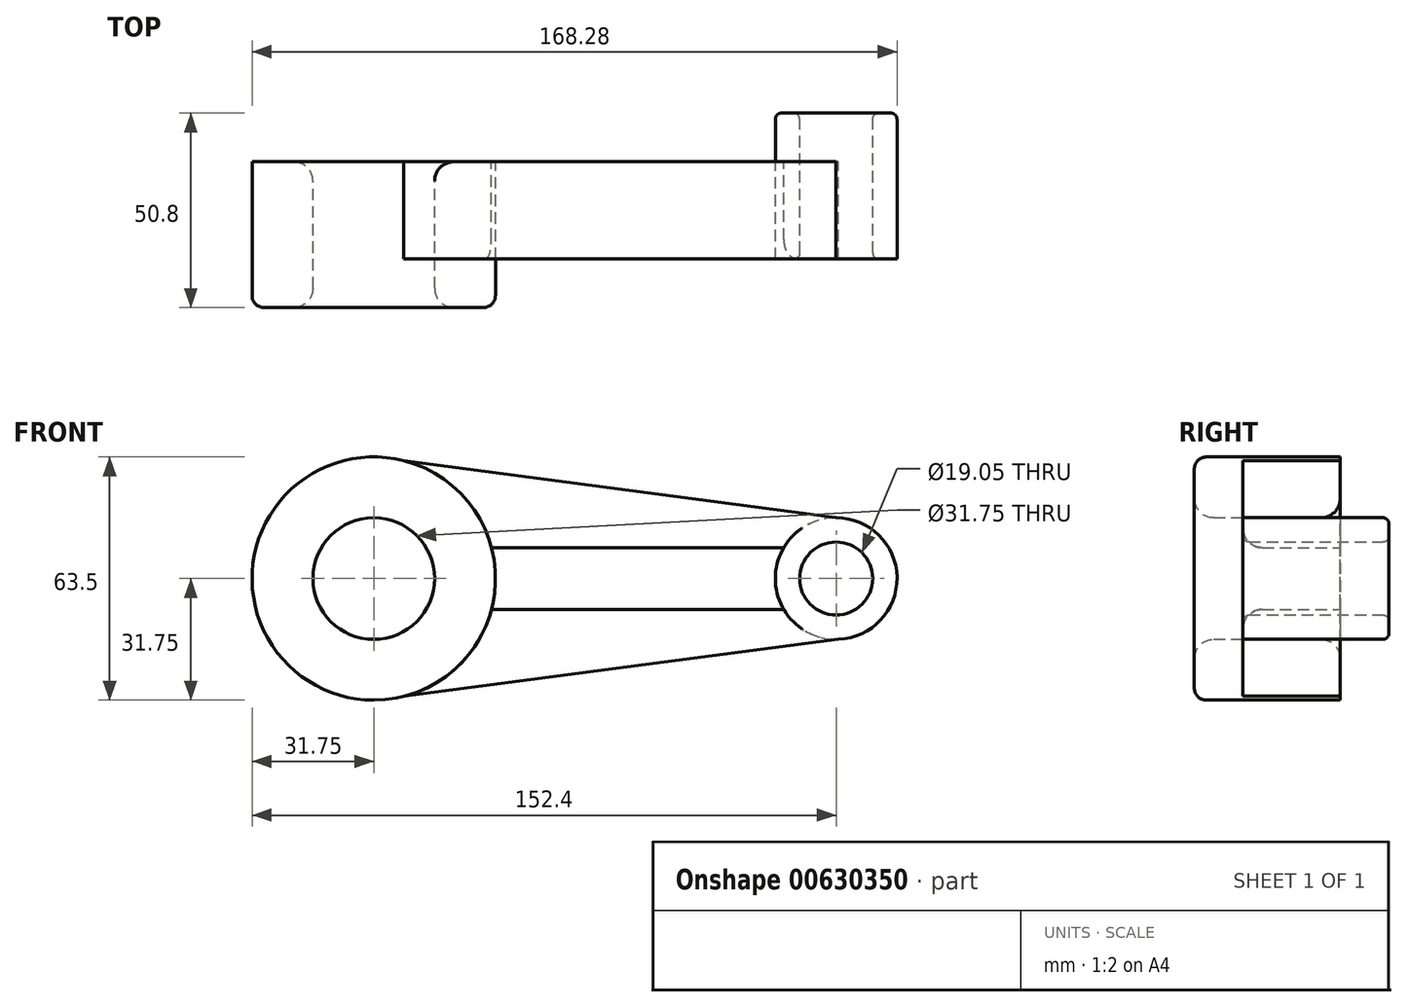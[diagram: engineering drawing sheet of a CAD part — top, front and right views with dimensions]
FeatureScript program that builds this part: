
annotation { "Feature Type Name" : "Feature", "Feature Type Description" : "" }
export const myFeature = defineFeature(function(context is Context, id is Id, definition is map)
    precondition{}
    {
        {
            var Q0;
            Q0=qCreatedBy(makeId("Front.planeOp"),FACE);
            var sketch = newSketch(context, id + "F0", { "sketchPlane" : qUnion([Q0])});
            skCircle(sketch, "E0", {"center": v(0, 0) * mm, "radius": 31.75 * mm});
            skCircle(sketch, "E1", {"center": v(120.65, 0) * mm, "radius": 15.88 * mm});
            skLineSegment(sketch, "E2", {"start": v(0.48, 31.75) * mm, "end": v(120.57, 15.87) * mm});
            skLineSegment(sketch, "E3", {"start": v(121.27, -15.86) * mm, "end": v(0.19, -31.75) * mm});
            skLineSegment(sketch, "E4.0", {"start": v(30.7, -8.06) * mm, "end": v(106.98, -8.06) * mm});
            skLineSegment(sketch, "E5.0", {"start": v(30.7, 8.06) * mm, "end": v(106.98, 8.06) * mm});
            skCircle(sketch, "E6", {"center": v(0, 0) * mm, "radius": 15.88 * mm});
            skCircle(sketch, "E7", {"center": v(120.65, 0) * mm, "radius": 9.53 * mm});
            skSolve(sketch);
        }
        {
            var Q0;
            Q0 = qSketchRegion(id + "F0", true);
            extrude(context, id + "F1", {"entities" : qUnion([Q0]), "depth" : 25.4 * mm, "offsetDistance" : 25.4 * mm});
        }
        {
            var Q0;
            Q0=makeQuery(id+"F1.opExtrude","CAP_FACE",FACE,{"disambiguationData":[OSD([sQuery(id+"F0.wireOp",EDGE,"E0"),sQuery(id+"F0.wireOp",EDGE,"E1"),sQuery(id+"F0.wireOp",EDGE,"E2"),sQuery(id+"F0.wireOp",EDGE,"E3"),sQuery(id+"F0.wireOp",EDGE,"E4.0"),sQuery(id+"F0.wireOp",EDGE,"E5.0"),sQuery(id+"F0.wireOp",EDGE,"E6"),sQuery(id+"F0.wireOp",EDGE,"E7")])],"isStart":false});
            var sketch = newSketch(context, id + "F2", { "sketchPlane" : qUnion([Q0])});
            skCircle(sketch, "E8", {"center": v(0, 0) * mm, "radius": 31.75 * mm});
            skCircle(sketch, "E9", {"center": v(0, 0) * mm, "radius": 15.88 * mm});
            skSolve(sketch);
        }
        {
            var Q0;
            Q0=makeQuery(id+"F1.opExtrude","CAP_FACE",FACE,{"disambiguationData":[OSD([sQuery(id+"F0.wireOp",EDGE,"E0"),sQuery(id+"F0.wireOp",EDGE,"E1"),sQuery(id+"F0.wireOp",EDGE,"E2"),sQuery(id+"F0.wireOp",EDGE,"E3"),sQuery(id+"F0.wireOp",EDGE,"E4.0"),sQuery(id+"F0.wireOp",EDGE,"E5.0"),sQuery(id+"F0.wireOp",EDGE,"E6"),sQuery(id+"F0.wireOp",EDGE,"E7")])],"isStart":true});
            var sketch = newSketch(context, id + "F3", { "sketchPlane" : qUnion([Q0])});
            skCircle(sketch, "E10", {"center": v(-120.65, 0) * mm, "radius": 9.53 * mm});
            skCircle(sketch, "E11", {"center": v(-120.65, 0) * mm, "radius": 15.88 * mm});
            skSolve(sketch);
        }
        {
            var Q0;
            Q0 = qSketchRegion(id + "F3", true);
            extrude(context, id + "F4", {"entities" : qUnion([Q0]), "operationType" : NewBodyOperationType.ADD, "depth" : 12.7 * mm, "offsetDistance" : 25.4 * mm});
        }
        {
            var Q0;
            Q0 = qSketchRegion(id + "F2", true);
            extrude(context, id + "F5", {"entities" : qUnion([Q0]), "operationType" : NewBodyOperationType.ADD, "depth" : 12.7 * mm, "offsetDistance" : 25.4 * mm});
        }
        {
            var Q0;
            Q0=makeQuery(id+"F1.opExtrude","CAP_EDGE",EDGE,{"disambiguationData":[OSD([sQuery(id+"F0.wireOp",EDGE,"E4.0")])],"isStart":false});
            var Q1;
            Q1=makeQuery(id+"F1.opExtrude","CAP_EDGE",EDGE,{"disambiguationData":[OSD([sQuery(id+"F0.wireOp",EDGE,"E5.0")])],"isStart":false});
            var Q2;
            {var subQ3=sQuery(id+"F0.wireOp",EDGE,"E3");var subQ7=sQuery(id+"F2.wireOp",EDGE,"E8");Q2=makeQuery(id+"F5.boolean.opBoolean","SPLIT",EDGE,{"disambiguationData":[TD([makeQuery(id+"F1.opExtrude","SWEPT_FACE",FACE,{"disambiguationData":[OSD([subQ3])]})])],"derivedFrom":makeQuery(id+"F5.opExtrude","CAP_EDGE",EDGE,{"disambiguationData":[OSD([subQ7])],"isStart":true})});}
            var Q3;
            {var subQ0=sQuery(id+"F0.wireOp",EDGE,"E2");var subQ1=sQuery(id+"F2.wireOp",EDGE,"E8");Q3=makeQuery(id+"F5.boolean.opBoolean","SPLIT",EDGE,{"disambiguationData":[TD([makeQuery(id+"F1.opExtrude","SWEPT_FACE",FACE,{"disambiguationData":[OSD([subQ0])]})])],"derivedFrom":makeQuery(id+"F5.opExtrude","CAP_EDGE",EDGE,{"disambiguationData":[OSD([subQ1])],"isStart":true})});}
            fillet(context, id + "F6", {"entities" : qUnion([Q0, Q1, Q2, Q3]), "radius" : 5.08 * mm, "tangentPropagation" : true, "allowEdgeOverflow" : false});
        }
        {
            var Q0;
            Q0=makeQuery(id+"F5.opExtrude","CAP_EDGE",EDGE,{"disambiguationData":[OSD([sQuery(id+"F2.wireOp",EDGE,"E8")])],"isStart":false});
            fillet(context, id + "F7", {"entities" : qUnion([Q0]), "radius" : 3.17 * mm, "tangentPropagation" : true, "allowEdgeOverflow" : false});
        }
        {
            var Q0;
            Q0=makeQuery(id+"F4.opExtrude","CAP_EDGE",EDGE,{"disambiguationData":[OSD([sQuery(id+"F3.wireOp",EDGE,"E11")])],"isStart":false});
            var Q1;
            Q1=makeQuery(id+"F4.opExtrude","CAP_EDGE",EDGE,{"disambiguationData":[OSD([sQuery(id+"F3.wireOp",EDGE,"E10")])],"isStart":false});
            var Q2;
            Q2=makeQuery(id+"F1.opExtrude","CAP_EDGE",EDGE,{"disambiguationData":[OSD([sQuery(id+"F0.wireOp",EDGE,"E7")])],"isStart":false});
            fillet(context, id + "F8", {"entities" : qUnion([Q0, Q1, Q2]), "radius" : 1.57 * mm, "tangentPropagation" : true, "allowEdgeOverflow" : false});
        }
        {
            var Q0;
            Q0=makeQuery(id+"F1.opExtrude","CAP_EDGE",EDGE,{"disambiguationData":[OSD([sQuery(id+"F0.wireOp",EDGE,"E6")])],"isStart":true});
            var Q1;
            Q1=makeQuery(id+"F5.opExtrude","CAP_EDGE",EDGE,{"disambiguationData":[OSD([sQuery(id+"F2.wireOp",EDGE,"E9")])],"isStart":false});
            fillet(context, id + "F9", {"entities" : qUnion([Q0, Q1]), "radius" : 5.08 * mm, "tangentPropagation" : true, "allowEdgeOverflow" : false});
        }
    });
